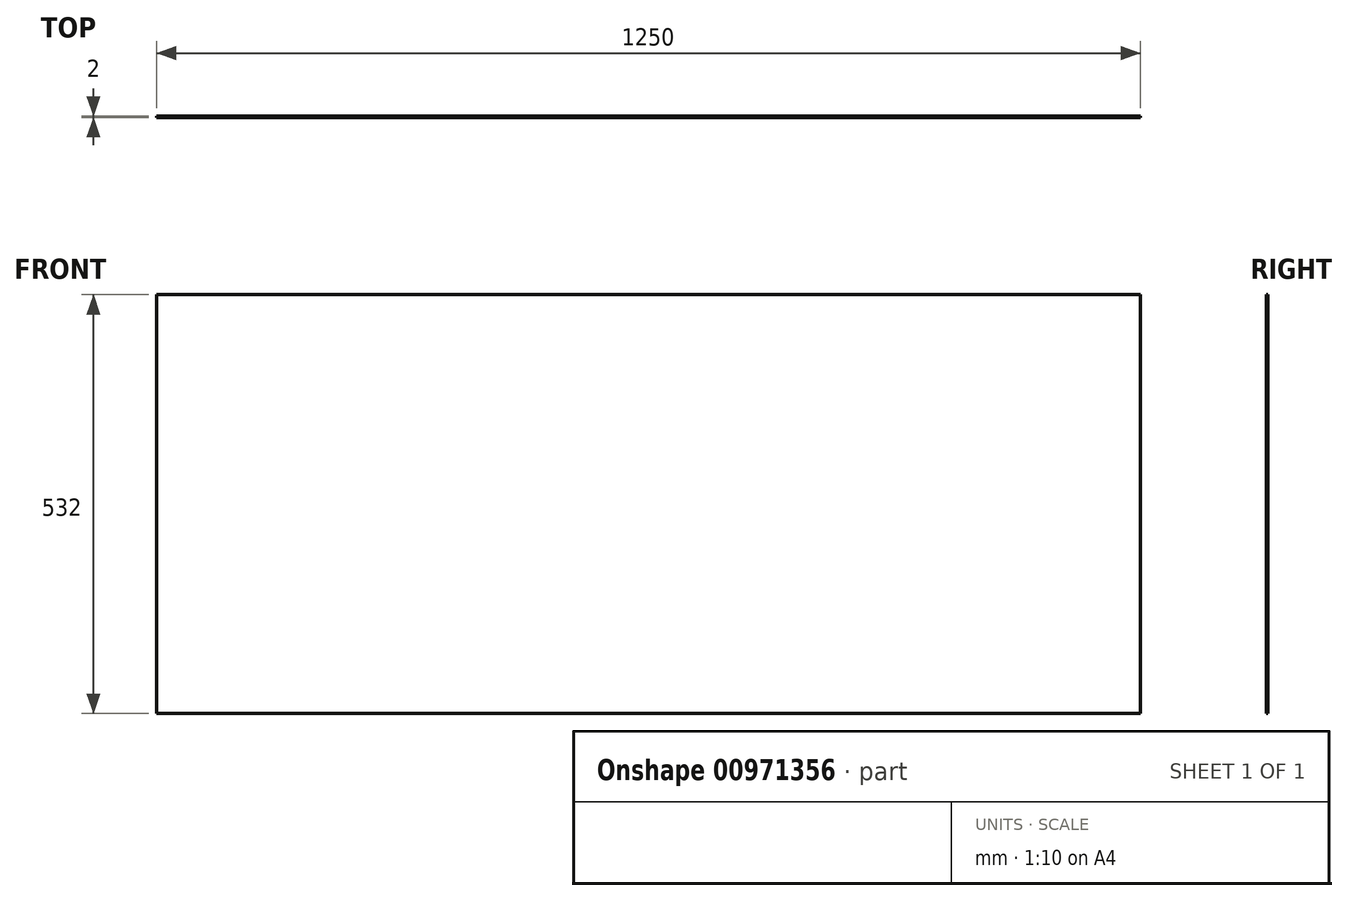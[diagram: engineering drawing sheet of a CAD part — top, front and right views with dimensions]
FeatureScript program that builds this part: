
annotation { "Feature Type Name" : "Feature", "Feature Type Description" : "" }
export const myFeature = defineFeature(function(context is Context, id is Id, definition is map)
    precondition{}
    {
        {
            var Q0;
            Q0=qCreatedBy(makeId("Front.planeOp"),FACE);
            var sketch = newSketch(context, id + "F0", { "sketchPlane" : qUnion([Q0])});
            skLineSegment(sketch, "E0.bottom", {"start": v(625, 266) * mm, "end": v(-625, 266) * mm});
            skLineSegment(sketch, "E0.top", {"start": v(625, -266) * mm, "end": v(-625, -266) * mm});
            skLineSegment(sketch, "E0.left", {"start": v(625, 266) * mm, "end": v(625, -266) * mm});
            skLineSegment(sketch, "E0.right", {"start": v(-625, 266) * mm, "end": v(-625, -266) * mm});
            skPoint(sketch, "E0.middle", {"position": v(0, 0) * mm});
            skSolve(sketch);
        }
        {
            var Q0;
            Q0=makeQuery(id+"F0.imprint","IMPRINT",FACE,{"disambiguationData":[TD([[makeQuery(id+"F0.imprint","IMPRINT",EDGE,{"derivedFrom":sQuery(id+"F0.wireOp",EDGE,"E0.bottom")}),1.0]])]});
            extrude(context, id + "F1", {"entities" : qUnion([Q0]), "depth" : 2 * mm, "offsetDistance" : 25 * mm});
        }
    });
